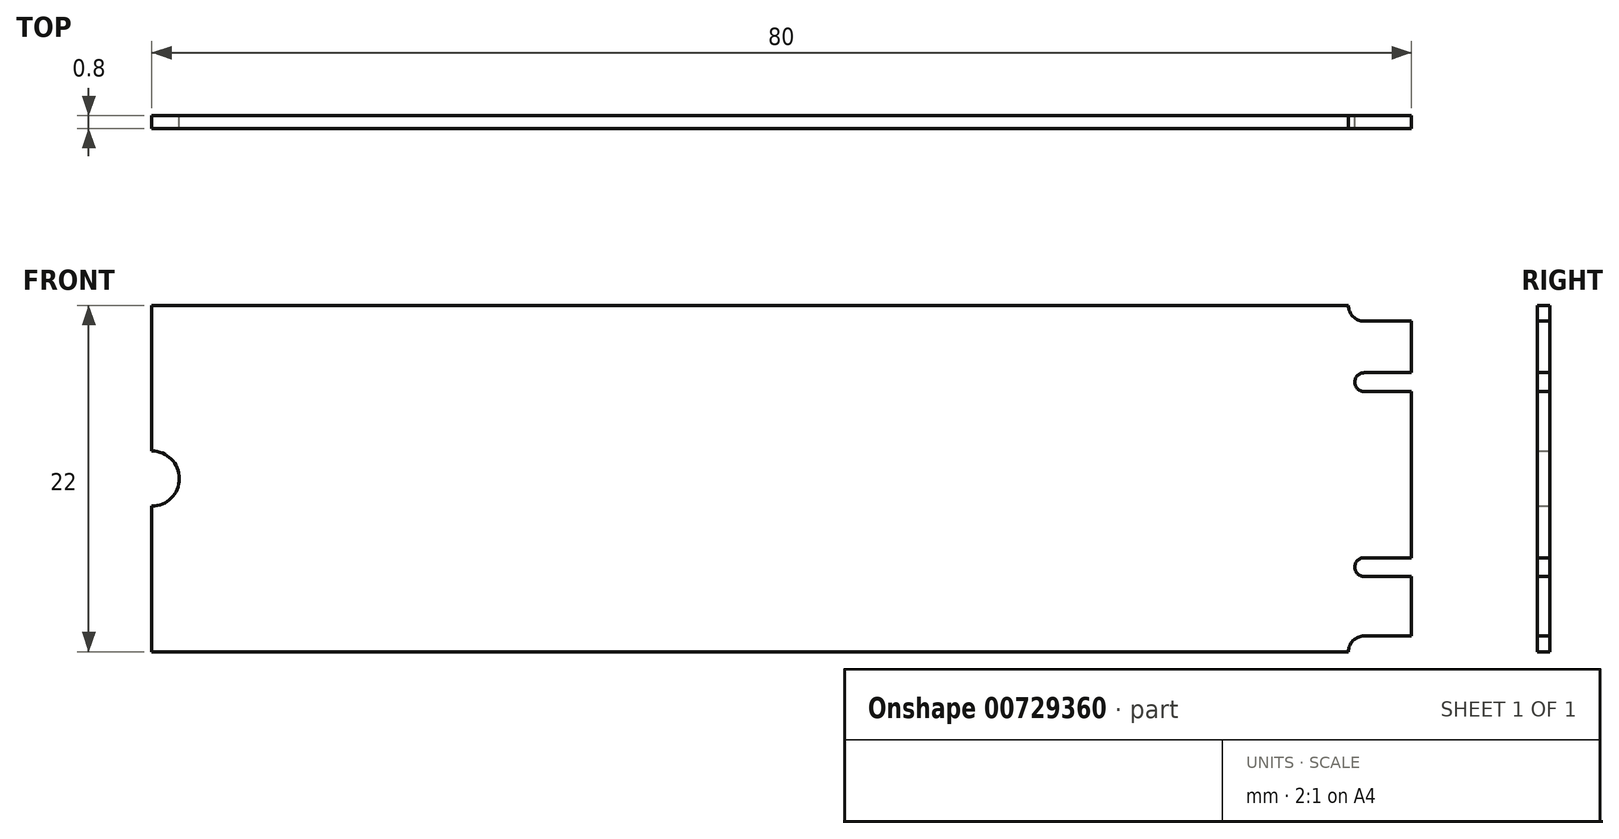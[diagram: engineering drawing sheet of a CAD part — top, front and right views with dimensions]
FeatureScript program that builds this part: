
annotation { "Feature Type Name" : "Feature", "Feature Type Description" : "" }
export const myFeature = defineFeature(function(context is Context, id is Id, definition is map)
    precondition{}
    {
        {
            var Q0;
            Q0=qCreatedBy(makeId("Front.planeOp"),FACE);
            var sketch = newSketch(context, id + "F0", { "sketchPlane" : qUnion([Q0])});
            skLineSegment(sketch, "E0.left", {"start": v(40, -10) * mm, "end": v(40, -6.22) * mm});
            skLineSegment(sketch, "E0.right", {"start": v(-40, -11) * mm, "end": v(-40, -1.75) * mm});
            skPoint(sketch, "E0.middle", {"position": v(0, 0) * mm});
            skLineSegment(sketch, "E1", {"start": v(-40, 0) * mm, "end": v(40, 0) * mm, "construction": true});
            skArc(sketch, "E2", {"start": v(-40, -3) * mm, "mid": v(-37, 0) * mm, "end": v(-40, 3) * mm});
            skArc(sketch, "E3", {"start": v(-40, -1.75) * mm, "mid": v(-38.25, 0) * mm, "end": v(-40, 1.75) * mm});
            skLineSegment(sketch, "E4", {"start": v(36, 11) * mm, "end": v(36, -11) * mm, "construction": true});
            skLineSegment(sketch, "E5", {"start": v(37, 10) * mm, "end": v(37, 6.72) * mm, "construction": true});
            skArc(sketch, "E6", {"start": v(36, 11) * mm, "mid": v(36.3, 10.3) * mm, "end": v(37, 10) * mm});
            skPoint(sketch, "E7", {"position": v(37, 10) * mm});
            skLineSegment(sketch, "E8", {"start": v(37, 10) * mm, "end": v(40, 10) * mm});
            skArc(sketch, "E9.MirrorC", {"start": v(36, -11) * mm, "mid": v(36.3, -10.3) * mm, "end": v(37, -10) * mm});
            skLineSegment(sketch, "E10.MirrorCS", {"start": v(37, -10) * mm, "end": v(40, -10) * mm});
            skPoint(sketch, "E11", {"position": v(37, 6.12) * mm});
            skArc(sketch, "E12", {"start": v(37, 6.72) * mm, "mid": v(36.4, 6.12) * mm, "end": v(37, 5.53) * mm});
            skPoint(sketch, "E13", {"position": v(37, 6.72) * mm});
            skPoint(sketch, "E14", {"position": v(37, 5.53) * mm});
            skPoint(sketch, "E15", {"position": v(37.6, 6.13) * mm});
            skLineSegment(sketch, "E16", {"start": v(37, 6.72) * mm, "end": v(40, 6.72) * mm});
            skLineSegment(sketch, "E17", {"start": v(37, 5.53) * mm, "end": v(40, 5.53) * mm});
            skPoint(sketch, "E18", {"position": v(37, -5.62) * mm});
            skArc(sketch, "E19", {"start": v(37, -5.03) * mm, "mid": v(36.4, -5.62) * mm, "end": v(37, -6.22) * mm});
            skPoint(sketch, "E20", {"position": v(36.4, -5.62) * mm});
            skPoint(sketch, "E21", {"position": v(37, -5.03) * mm});
            skPoint(sketch, "E22", {"position": v(37.6, -5.62) * mm});
            skPoint(sketch, "E23", {"position": v(37, -6.22) * mm});
            skLineSegment(sketch, "E24", {"start": v(37, -5.03) * mm, "end": v(40, -5.03) * mm});
            skLineSegment(sketch, "E25", {"start": v(37, -6.22) * mm, "end": v(40, -6.22) * mm});
            skLineSegment(sketch, "E26", {"start": v(36.4, -5.62) * mm, "end": v(36.4, -2.77) * mm, "construction": true});
            skLineSegment(sketch, "E27.trimOffspring", {"start": v(36, 11) * mm, "end": v(-40, 11) * mm});
            skLineSegment(sketch, "E28.trimOffspring", {"start": v(37, 5.53) * mm, "end": v(37, -5.03) * mm, "construction": true});
            skLineSegment(sketch, "E29.trimOffspring", {"start": v(36.4, 6.12) * mm, "end": v(26.22, 6.12) * mm, "construction": true});
            skLineSegment(sketch, "E30.trimOffspring", {"start": v(40, 6.73) * mm, "end": v(40, 11) * mm});
            skLineSegment(sketch, "E31.trimOffspring", {"start": v(37, -6.22) * mm, "end": v(37, -10) * mm, "construction": true});
            skLineSegment(sketch, "E32.trimOffspring", {"start": v(36.4, -5.62) * mm, "end": v(28.02, -5.63) * mm, "construction": true});
            skLineSegment(sketch, "E33.trimOffspring", {"start": v(40, -5.03) * mm, "end": v(40, 5.53) * mm});
            skLineSegment(sketch, "E34.trimOffspring", {"start": v(36, -11) * mm, "end": v(-40, -11) * mm});
            skPoint(sketch, "E35.orphan", {"position": v(40, -11) * mm});
            skLineSegment(sketch, "E36.trimOffspring", {"start": v(-40, 1.75) * mm, "end": v(-40, 11) * mm});
            skSolve(sketch);
        }
        {
            var Q0;
            Q0 = qSketchRegion(id + "F0", true);
            extrude(context, id + "F1", {"entities" : qUnion([Q0]), "depth" : .80 * mm, "offsetDistance" : 25 * mm});
        }
    });
